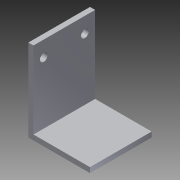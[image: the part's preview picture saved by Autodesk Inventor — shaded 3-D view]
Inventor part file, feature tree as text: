
AUTODESK INVENTOR PART (.ipt)
format: ipt  version: 2013 (Build 170138000, 138)  size: 87,552 bytes
history: native  units: in
note: dims shown in document units (in); Inventor stores cm internally (conversion verified against a paired STEP export)
features: extrude x2, sketch x2
ambient origin geometry x8: Origin, YZ Plane, XZ Plane, XY Plane, X Axis, Y Axis, Z Axis, Center Point
bodies: Solid1 (feature_tree)
feature tree (4):
  extrude  "Extrusion1"  Depth=2.0in
  extrude  "Extrusion2"  Depth=1.5in TaperAngle=0.0deg
  sketch  "Sketch1"  dims[d0=1.5in d1=2.0in]
  sketch  "Sketch2"  dims[d2=0.125in d3=1.5in d4=0.0in d5=1.0in d6=0.375in d7=0.1875in d8=0.1875in d9=1.5in d10=0.0in]
